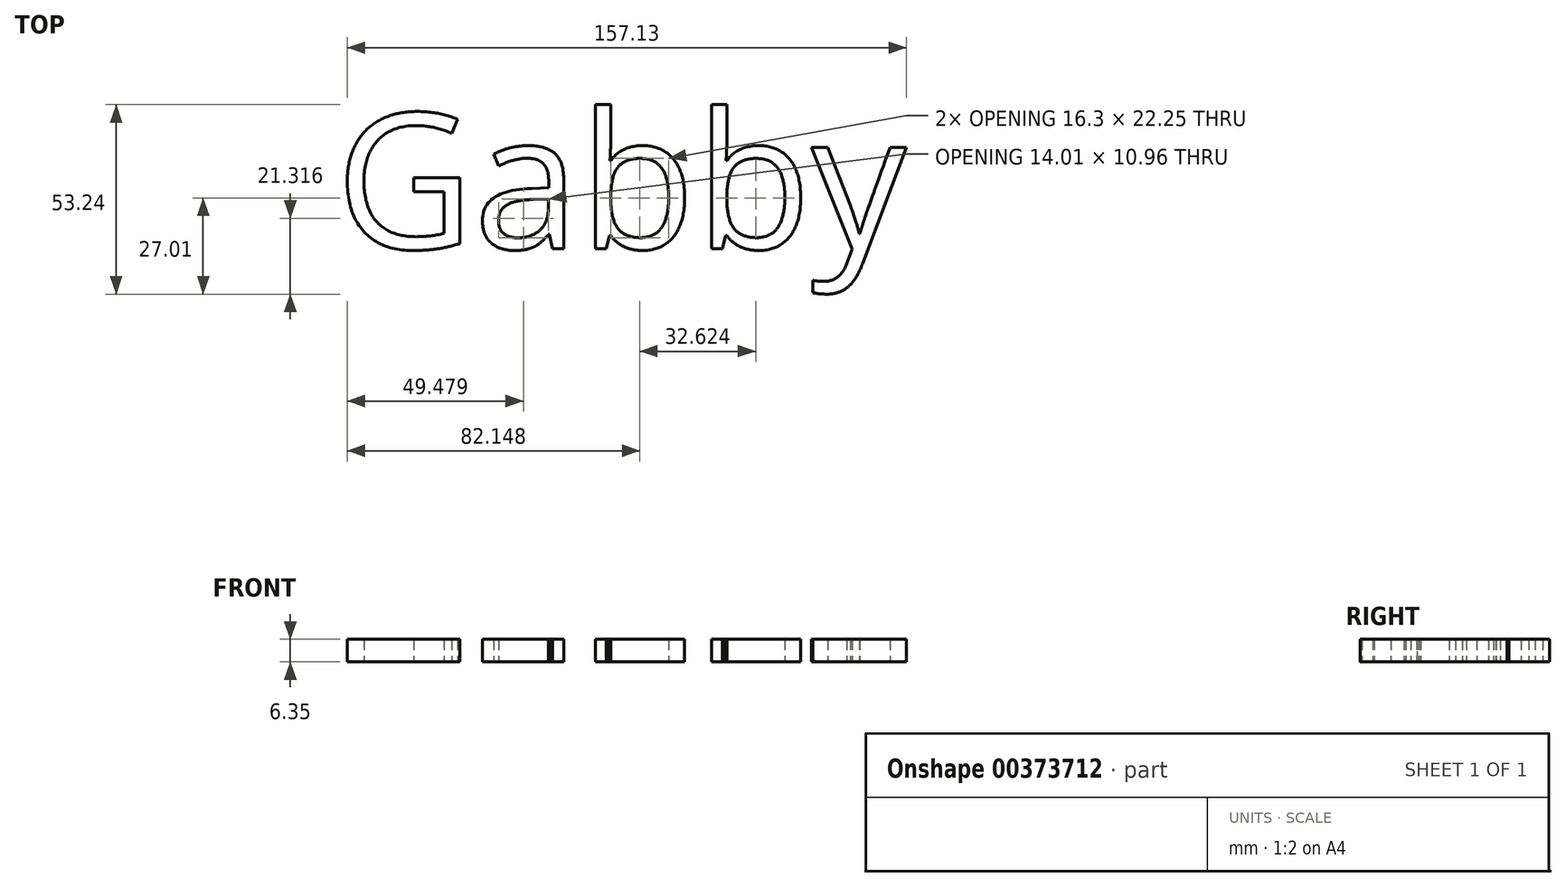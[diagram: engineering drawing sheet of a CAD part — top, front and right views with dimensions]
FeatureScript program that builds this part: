
annotation { "Feature Type Name" : "Feature", "Feature Type Description" : "" }
export const myFeature = defineFeature(function(context is Context, id is Id, definition is map)
    precondition{}
    {
        {
            var Q0;
            Q0=qCreatedBy(makeId("Top.planeOp"),FACE);
            var sketch = newSketch(context, id + "F0", { "sketchPlane" : qUnion([Q0])});
            skText(sketch, "E0", { "text": "Gabby", "fontName": "OpenSans-Regular.ttf"});
            const initialGuessF0  = {"E0": [-0.02982, -0.0182, 1, 0, 0.03833]};
            skSetInitialGuess(sketch, initialGuessF0);
            skSolve(sketch);
        }
        {
            var Q0;
            Q0 = qSketchRegion(id + "F0", true);
            extrude(context, id + "F1", {"entities" : qUnion([Q0]), "depth" : 6.35 * mm});
        }
    });
